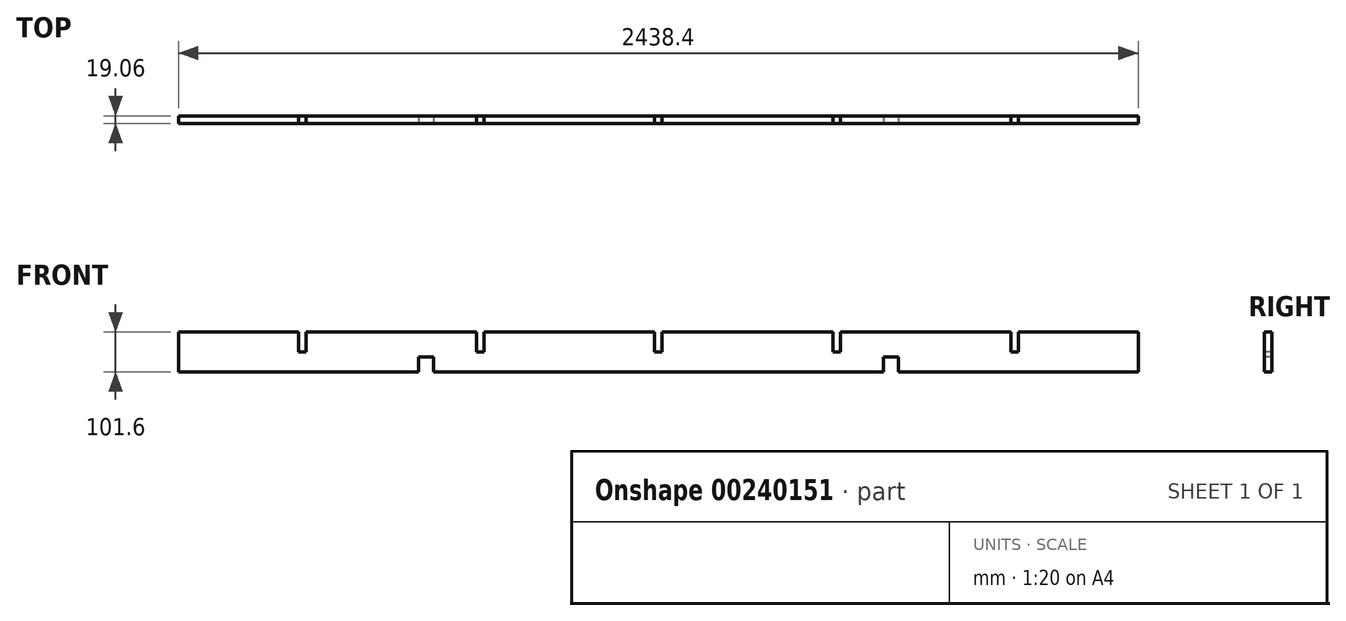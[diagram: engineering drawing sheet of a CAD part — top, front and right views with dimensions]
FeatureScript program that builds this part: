
annotation { "Feature Type Name" : "Feature", "Feature Type Description" : "" }
export const myFeature = defineFeature(function(context is Context, id is Id, definition is map)
    precondition{}
    {
        {
            var Q0;
            Q0=qCreatedBy(makeId("Top.planeOp"),FACE);
            var sketch = newSketch(context, id + "F0", { "sketchPlane" : qUnion([Q0])});
            skLineSegment(sketch, "E0", {"start": v(1219.2, 0) * mm, "end": v(1219.2, 9.53) * mm});
            skLineSegment(sketch, "E1", {"start": v(1219.2, 9.53) * mm, "end": v(-1219.2, 9.53) * mm});
            skLineSegment(sketch, "E2", {"start": v(-1219.2, 9.53) * mm, "end": v(-1219.2, 0) * mm});
            skLineSegment(sketch, "E3.MirrorCS", {"start": v(-1219.2, -9.53) * mm, "end": v(-1219.2, 0) * mm});
            skLineSegment(sketch, "E4.MirrorCS", {"start": v(1219.2, -9.53) * mm, "end": v(-1219.2, -9.53) * mm});
            skLineSegment(sketch, "E5.MirrorCS", {"start": v(1219.2, 0) * mm, "end": v(1219.2, -9.53) * mm});
            skSolve(sketch);
        }
        {
            var Q0;
            Q0 = qSketchRegion(id + "F0", true);
            extrude(context, id + "F1", {"entities" : qUnion([Q0]), "oppositeDirection" : true, "depth" : 101.6 * mm});
        }
        {
            var Q0;
            Q0=makeQuery(id+"F1.opExtrude","SWEPT_FACE",FACE,{"disambiguationData":[OSD([sQuery(id+"F0.wireOp",EDGE,"E4.MirrorCS")])]});
            var sketch = newSketch(context, id + "F2", { "sketchPlane" : qUnion([Q0])});
            skLineSegment(sketch, "E6", {"start": v(1219.2, -101.6) * mm, "end": v(1219.2, -259.57) * mm, "construction": true});
            skLineSegment(sketch, "E7", {"start": v(1219.2, -259.57) * mm, "end": v(609.6, -259.57) * mm, "construction": true});
            skLineSegment(sketch, "E8", {"start": v(609.6, -101.6) * mm, "end": v(609.6, -63.5) * mm});
            skLineSegment(sketch, "E9", {"start": v(609.6, -63.5) * mm, "end": v(571.5, -63.5) * mm});
            skLineSegment(sketch, "E10", {"start": v(571.5, -63.5) * mm, "end": v(571.5, -101.6) * mm});
            skLineSegment(sketch, "E11.MirrorCS", {"start": v(-609.6, -101.6) * mm, "end": v(-609.6, -63.5) * mm});
            skLineSegment(sketch, "E12.MirrorCS", {"start": v(-609.6, -63.5) * mm, "end": v(-571.5, -63.5) * mm});
            skLineSegment(sketch, "E13.MirrorCS", {"start": v(-571.5, -63.5) * mm, "end": v(-571.5, -101.6) * mm});
            skLineSegment(sketch, "E14", {"start": v(0, -101.6) * mm, "end": v(0, 153.9) * mm, "construction": true});
            skLineSegment(sketch, "E15", {"start": v(0, 0) * mm, "end": v(-9.53, 0) * mm});
            skLineSegment(sketch, "E16", {"start": v(-9.53, 0) * mm, "end": v(-9.52, -50.8) * mm});
            skLineSegment(sketch, "E17", {"start": v(-9.52, -50.8) * mm, "end": v(0, -50.8) * mm});
            skLineSegment(sketch, "E18.MirrorCS", {"start": v(0, 0) * mm, "end": v(9.53, 0) * mm});
            skLineSegment(sketch, "E19.MirrorCS", {"start": v(9.53, 0) * mm, "end": v(9.52, -50.8) * mm});
            skLineSegment(sketch, "E20.MirrorCS", {"start": v(9.52, -50.8) * mm, "end": v(0, -50.8) * mm});
            skLineSegment(sketch, "E21", {"start": v(1219.2, 0) * mm, "end": v(1219.2, 101.6) * mm, "construction": true});
            skLineSegment(sketch, "E22", {"start": v(1219.2, 101.6) * mm, "end": v(914.4, 101.6) * mm, "construction": true});
            skLineSegment(sketch, "E23", {"start": v(914.4, 0) * mm, "end": v(914.4, -50.8) * mm});
            skLineSegment(sketch, "E24", {"start": v(914.4, -50.8) * mm, "end": v(895.35, -50.8) * mm});
            skLineSegment(sketch, "E25", {"start": v(895.35, -50.8) * mm, "end": v(895.35, 0) * mm});
            skLineSegment(sketch, "E26", {"start": v(895.35, 0) * mm, "end": v(914.4, 0) * mm});
            skLineSegment(sketch, "E27.MirrorCS", {"start": v(-895.35, 0) * mm, "end": v(-914.4, 0) * mm});
            skLineSegment(sketch, "E28.MirrorCS", {"start": v(-895.35, -50.8) * mm, "end": v(-895.35, 0) * mm});
            skLineSegment(sketch, "E29.MirrorCS", {"start": v(-914.4, -50.8) * mm, "end": v(-895.35, -50.8) * mm});
            skLineSegment(sketch, "E30.MirrorCS", {"start": v(-914.4, 0) * mm, "end": v(-914.4, -50.8) * mm});
            skLineSegment(sketch, "E31", {"start": v(-904.88, 0) * mm, "end": v(-904.88, 79.53) * mm, "construction": true});
            skLineSegment(sketch, "E32", {"start": v(-904.88, 79.53) * mm, "end": v(0, 79.53) * mm, "construction": true});
            skLineSegment(sketch, "E33", {"start": v(-452.44, 79.53) * mm, "end": v(-452.44, 0) * mm, "construction": true});
            skLineSegment(sketch, "E34", {"start": v(-452.44, 0) * mm, "end": v(-442.91, 0) * mm});
            skLineSegment(sketch, "E35", {"start": v(-442.91, 0) * mm, "end": v(-442.91, -50.8) * mm});
            skLineSegment(sketch, "E36", {"start": v(-442.91, -50.8) * mm, "end": v(-461.96, -50.8) * mm});
            skLineSegment(sketch, "E37", {"start": v(-461.96, -50.8) * mm, "end": v(-461.96, 0) * mm});
            skLineSegment(sketch, "E38", {"start": v(-461.96, 0) * mm, "end": v(-452.44, 0) * mm});
            skLineSegment(sketch, "E39.MirrorCS", {"start": v(452.44, 0) * mm, "end": v(442.91, 0) * mm});
            skLineSegment(sketch, "E40.MirrorCS", {"start": v(461.96, 0) * mm, "end": v(452.44, 0) * mm});
            skLineSegment(sketch, "E41.MirrorCS", {"start": v(461.96, -50.8) * mm, "end": v(461.96, 0) * mm});
            skLineSegment(sketch, "E42.MirrorCS", {"start": v(442.91, -50.8) * mm, "end": v(461.96, -50.8) * mm});
            skLineSegment(sketch, "E43.MirrorCS", {"start": v(442.91, 0) * mm, "end": v(442.91, -50.8) * mm});
            skSolve(sketch);
        }
        {
            var Q0;
            {var subQ0=sQuery(id+"F2.wireOp",EDGE,"E8");Q0=makeQuery(id+"F2.imprint","IMPRINT",FACE,{"disambiguationData":[TD([[makeQuery(id+"F2.imprint","IMPRINT",EDGE,{"derivedFrom":subQ0}),1.0]])]});}
            extrude(context, id + "F3", {"entities" : qUnion([Q0]), "operationType" : NewBodyOperationType.REMOVE, "oppositeDirection" : true, "depth" : 25.4 * mm});
        }
        {
            var Q0;
            {var subQ0=sQuery(id+"F2.wireOp",EDGE,"E11.MirrorCS");Q0=makeQuery(id+"F2.imprint","IMPRINT",FACE,{"disambiguationData":[TD([[makeQuery(id+"F2.imprint","IMPRINT",EDGE,{"derivedFrom":subQ0}),-1.0]])]});}
            extrude(context, id + "F4", {"entities" : qUnion([Q0]), "operationType" : NewBodyOperationType.REMOVE, "oppositeDirection" : true, "depth" : 25.4 * mm});
        }
        {
            var Q0;
            Q0=makeQuery(id+"F2.imprint","IMPRINT",FACE,{"disambiguationData":[TD([[makeQuery(id+"F2.imprint","IMPRINT",EDGE,{"derivedFrom":sQuery(id+"F2.wireOp",EDGE,"E27.MirrorCS")}),1.0]])]});
            var Q1;
            Q1=makeQuery(id+"F2.imprint","IMPRINT",FACE,{"disambiguationData":[TD([[makeQuery(id+"F2.imprint","IMPRINT",EDGE,{"derivedFrom":sQuery(id+"F2.wireOp",EDGE,"E34")}),1.0]])]});
            var Q2;
            Q2=makeQuery(id+"F2.imprint","IMPRINT",FACE,{"disambiguationData":[TD([[makeQuery(id+"F2.imprint","IMPRINT",EDGE,{"derivedFrom":sQuery(id+"F2.wireOp",EDGE,"E15")}),1.0]])]});
            var Q3;
            Q3=makeQuery(id+"F2.imprint","IMPRINT",FACE,{"disambiguationData":[TD([[makeQuery(id+"F2.imprint","IMPRINT",EDGE,{"derivedFrom":sQuery(id+"F2.wireOp",EDGE,"E39.MirrorCS")}),1.0]])]});
            var Q4;
            Q4=makeQuery(id+"F2.imprint","IMPRINT",FACE,{"disambiguationData":[TD([[makeQuery(id+"F2.imprint","IMPRINT",EDGE,{"derivedFrom":sQuery(id+"F2.wireOp",EDGE,"E23")}),-1.0]])]});
            extrude(context, id + "F5", {"entities" : qUnion([Q0, Q1, Q2, Q3, Q4]), "operationType" : NewBodyOperationType.REMOVE, "oppositeDirection" : true, "depth" : 25.4 * mm});
        }
    });
